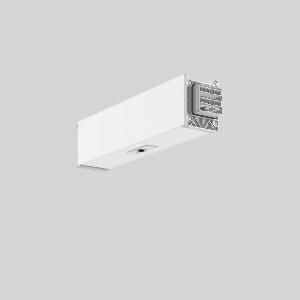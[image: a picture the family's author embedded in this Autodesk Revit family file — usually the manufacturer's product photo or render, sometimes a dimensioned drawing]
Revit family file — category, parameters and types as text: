
# Revit family: linedo_sensormodule_2-5_m_9503s1_002_400_000_8183
name_source: partatom
category: Lighting Fixtures
units: mm (PartAtom-declared; Revit-internal decimal feet)

## family parameters
Cut with Voids When Loaded = No
Host = Face
Light Source = No
Part Type = Normal
Room Calculation Point = No
Round Connector Dimension = Use Diameter
Shared = No

## types (1)
- LINEDO Sensormodule 2-5 m
    Apparent Load = 0 VA
    Default Elevation = 1800 mm
    Description = Series: LINEDO
Module including Passive Infrared (PIR) sensor for movement and ambient light. System profile made of aluminium extrusion profile, powder-coated. Simple, tool-free installation of system profiles using separate accessories for cable, chain or ceiling suspension. Tool-free connection and mechanical connectors to secure. 14-poles LINEDO connector (5 x 2.5 mm² / 9 x 1.5 mm²) for additional applications in light management or for the integration of emergency lighting. Phase can be set via patended bridge without opening the luminaire. Pre-assembled connector for DALI line. Light and movement sensor: Housing of non-flammable, halogen-free plastic (polycarbonate). Presence detection with passive IR element. Presence detection range adjustable via integrated shutters between 40° and 90°. Detection range: 6 m. Light sensor range: 20-800 lx (measured at the sensor). Function display with two-colour LED. Installation height: 2-5 m. Example of use: Monitoring of low ceiling rooms and rack storage where the installation height is normal. Please order supply module, connection and mounting accessories separately. 
Colour: traffic white, matt (RAL 9016)
Length: 330 mm
Width: 58 mm
Height: 76 mm
Weight: 770 g
Type of Installation: Recessed mounting
    Height = 77 mm
    Lamp = 0 x
    Length = 331 mm
    Luminous efficacy = 0 lm/W
    Manufacturer = RZB
    ModVariant = No
    Model = 9503S1.002.400.000
    Mounting Place = Ceiling
    Mounting Type = Surface mounted, Pendant
    Number of Poles = 1
    OnlyDefault = Yes
    Power Factor = 1
    Product Name = LINEDO Sensormodule 2-5 m
    Product group = Surface mounted continuous line luminaire system
    ProductGroupID = 310
    Protection Class = Protection class I
    Protection Degree = IP 20
    RLX_Detail_Level = 1
    RLX_Emergency_Light_Flux = 0 lm
    RLX_Emergency_Type = 0
    RLX_Emergency_Type_DB = No
    RlxData = <blob elided: 21805 chars, md5=3bf356ca>
    Standby Power = 0 W
    System Light Flux = 0 lm
    System Power = 0 W
    Type Comments = Product without accessories
    Type Image = 9503s1.002.400.000.jpg
    URL = http://relux.com
    VarID = ---
    Voltage = 230 V
    Voltage Range = 220-240 V
    Weight = 0.00 kg
    Width = 58 mm

## geometry (parser evidence)
native form markers: Blend x4, Sweep x12
no freeform markers — native parametric forms only
